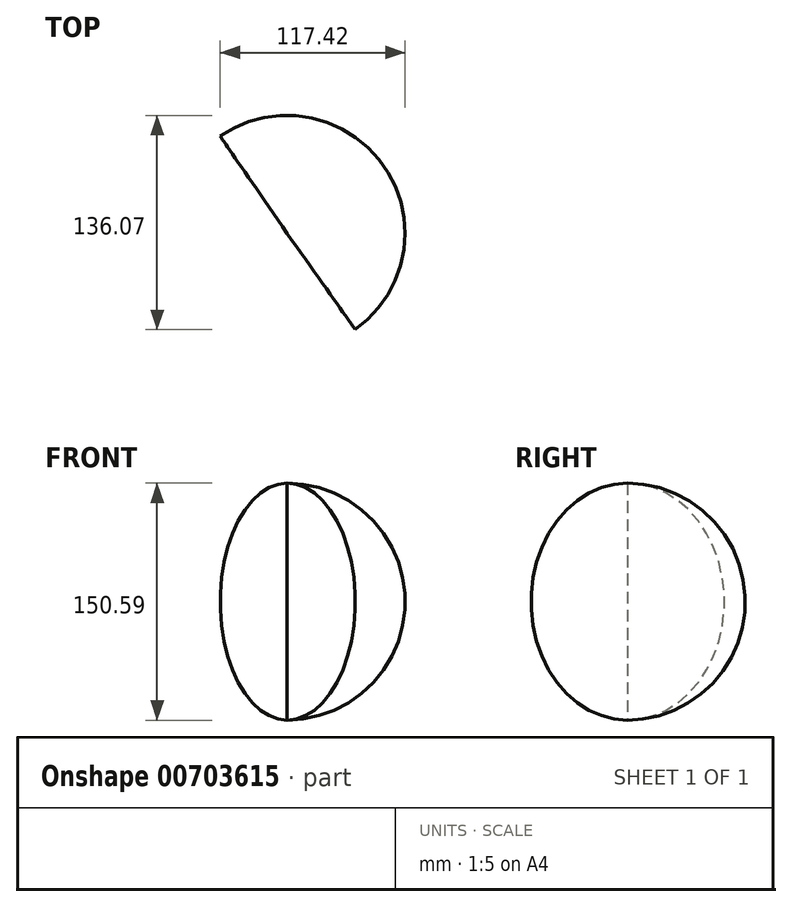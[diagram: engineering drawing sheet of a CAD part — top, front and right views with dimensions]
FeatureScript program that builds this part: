
annotation { "Feature Type Name" : "Feature", "Feature Type Description" : "" }
export const myFeature = defineFeature(function(context is Context, id is Id, definition is map)
    precondition{}
    {
        {
            var Q0;
            Q0=qCreatedBy(makeId("Front.planeOp"),FACE);
            var sketch = newSketch(context, id + "F0", { "sketchPlane" : qUnion([Q0])});
            skLineSegment(sketch, "E0", {"start": v(0, 75.01) * mm, "end": v(0, -75.58) * mm});
            skArc(sketch, "E1", {"start": v(0, -75.58) * mm, "mid": v(74.92, -0.28) * mm, "end": v(0, 75.01) * mm});
            skArc(sketch, "E2", {"start": v(0, -50.93) * mm, "mid": v(51.1, -2.25) * mm, "end": v(0, 46.44) * mm});
            skArc(sketch, "E3", {"start": v(0, -14.18) * mm, "mid": v(12.44, -0.49) * mm, "end": v(0, 13.2) * mm});
            skSolve(sketch);
        }
        {
            var Q0;
            Q0 = qSketchRegion(id + "F0", true);
            var Q1;
            Q1=sQuery(id+"F0.wireOp",EDGE,"E0");
            revolve(context, id + "F1", {"surfaceOperationType" : NewSurfaceOperationType.NEW, "entities" : qUnion([Q0]), "axis" : qUnion([Q1]), "revolveType" : RevolveType.TWO_DIRECTIONS, "angle" : 54.7 * degree, "angleBack" : 235.44 * degree});
        }
    });
